# Revit family: Krowne_HS-7_WallMount_HandSink
name_source: partatom
category: Plumbing Fixtures
revit_build: Autodesk Revit 2018 (Build: 20190510_1515(x64)
units: mm (PartAtom-declared; Revit-internal decimal feet)

## family parameters
Always vertical = Yes
Cut with Voids When Loaded = No
OmniClass Number = 23.40.40.14.24.11
OmniClass Title = Bar Equipment
Part Type = Normal
Room Calculation Point = No
Round Connector Dimension = Use Diameter
Shared = No
Work Plane-Based = No

## types (1)
- DefaultType
    Assembly Code = E1090320
    CSI MasterFormat = 11 46 13
    Cold Water Connection Height = 31.50"
    Cold Water Size = 1"
    Depth = 15.00"
    Description = Wall Mount Hand Sink
    Direct Waste Connection Height = 20.00"
    Direct Waste Size = 2"
    Foodservice Equipment Identifier = Yes
    Hot Water Connection Height = 31.50"
    Hot Water Size = 1"
    Hot Water Temperature = 100 °F
    KCL SpecSheet URL = http://kclweb.kclcad.com
    KCLRef = KCL2C9,,00009029-0000-0000-0000-000000000307,KR,HS-7 ,636965904281654080,3886adcb-6b9a-480a-8a8b-3ff8efbdc1c7,9a44e387-83e8-43a0-a647-0742fa641341
    Manufacturer = Krowne Metal
    Model = HS-7
    Sink Depth = 10.00"
    Sink Width = 10.00"
    URL = www.krowne.com
    Weight in Pounds = 42
    Width = 16.00"

## geometry (parser evidence)
native form markers: Blend x4, Sweep x1
no freeform markers — native parametric forms only
